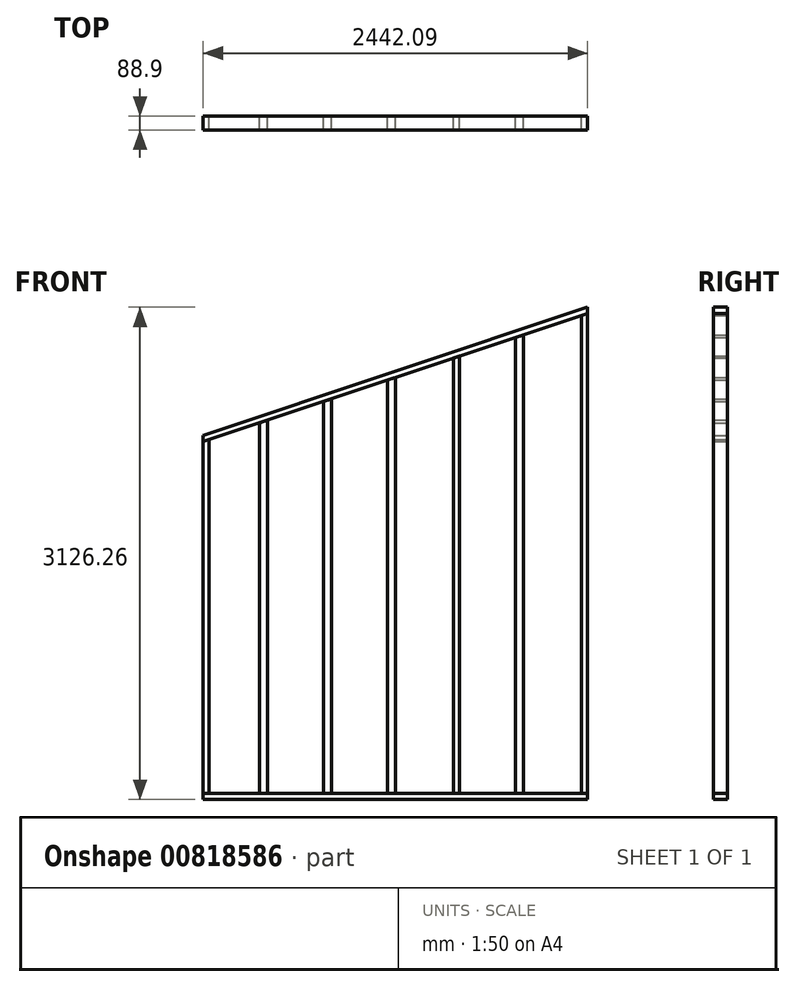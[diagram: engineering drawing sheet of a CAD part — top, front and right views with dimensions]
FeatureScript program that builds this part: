
annotation { "Feature Type Name" : "Feature", "Feature Type Description" : "" }
export const myFeature = defineFeature(function(context is Context, id is Id, definition is map)
    precondition{}
    {
        {
            var Q0;
            Q0=qCreatedBy(makeId("Front.planeOp"),FACE);
            var sketch = newSketch(context, id + "F0", { "sketchPlane" : qUnion([Q0])});
            skPoint(sketch, "E0", {"position": v(1489.55, 1139.12) * mm});
            skLineSegment(sketch, "E1", {"start": v(-952.54, 325.1) * mm, "end": v(1489.55, 1139.12) * mm});
            skLineSegment(sketch, "E2", {"start": v(1489.55, 1139.12) * mm, "end": v(1489.55, -1987.14) * mm});
            skLineSegment(sketch, "E3.0", {"start": v(-952.54, 284.93) * mm, "end": v(1489.55, 1098.96) * mm});
            skLineSegment(sketch, "E3.1", {"start": v(1451.45, 1086.26) * mm, "end": v(1451.45, -1949.04) * mm});
            skLineSegment(sketch, "E4.trimOffspring", {"start": v(1083.15, 963.5) * mm, "end": v(1083.15, -1949.04) * mm});
            skLineSegment(sketch, "E5.trimOffspring", {"start": v(1032.35, 946.56) * mm, "end": v(1032.35, -1949.04) * mm});
            skLineSegment(sketch, "E6.trimOffspring", {"start": v(676.75, 828.03) * mm, "end": v(676.75, -1949.04) * mm});
            skLineSegment(sketch, "E7.trimOffspring", {"start": v(219.55, 675.63) * mm, "end": v(219.55, -1949.04) * mm});
            skLineSegment(sketch, "E8.trimOffspring", {"start": v(270.35, 692.56) * mm, "end": v(270.35, -1949.04) * mm});
            skLineSegment(sketch, "E9.trimOffspring", {"start": v(-136.05, 557.1) * mm, "end": v(-136.05, -1949.04) * mm});
            skLineSegment(sketch, "E10.trimOffspring", {"start": v(-186.85, 540.16) * mm, "end": v(-186.85, -1949.04) * mm});
            skLineSegment(sketch, "E11.trimOffspring", {"start": v(-542.45, 421.63) * mm, "end": v(-542.45, -1949.04) * mm});
            skLineSegment(sketch, "E12.trimOffspring", {"start": v(-593.25, 404.7) * mm, "end": v(-593.25, -1949.04) * mm});
            skLineSegment(sketch, "E13.0", {"start": v(1489.55, -1949.04) * mm, "end": v(-952.54, -1949.04) * mm});
            skLineSegment(sketch, "E14.0", {"start": v(1489.55, -1987.14) * mm, "end": v(-952.54, -1987.14) * mm});
            skLineSegment(sketch, "E15.trimOffspring", {"start": v(-952.54, -1987.14) * mm, "end": v(-952.54, 325.1) * mm});
            skLineSegment(sketch, "E16.0", {"start": v(638.65, 815.33) * mm, "end": v(638.65, -1949.04) * mm});
            skLineSegment(sketch, "E17.0", {"start": v(-914.44, -1949.04) * mm, "end": v(-914.44, 297.63) * mm});
            skSolve(sketch);
        }
        {
            var Q0;
            {var subQ5=sQuery(id+"F0.wireOp",EDGE,"E3.1");Q0=makeQuery(id+"F0.imprint","IMPRINT",FACE,{"disambiguationData":[TD([[makeQuery(id+"F0.imprint","IMPRINT",EDGE,{"derivedFrom":subQ5}),1.0]])]});}
            var Q1;
            {var subQ3=sQuery(id+"F0.wireOp",EDGE,"E15.trimOffspring");Q1=makeQuery(id+"F0.imprint","IMPRINT",FACE,{"disambiguationData":[TD([[makeQuery(id+"F0.imprint","IMPRINT",EDGE,{"derivedFrom":subQ3}),1.0]])]});}
            var Q2;
            {var subQ0=sQuery(id+"F0.wireOp",EDGE,"E11.trimOffspring");Q2=makeQuery(id+"F0.imprint","IMPRINT",FACE,{"disambiguationData":[TD([[makeQuery(id+"F0.imprint","IMPRINT",EDGE,{"derivedFrom":subQ0}),-1.0]])]});}
            var Q3;
            {var subQ0=sQuery(id+"F0.wireOp",EDGE,"E9.trimOffspring");Q3=makeQuery(id+"F0.imprint","IMPRINT",FACE,{"disambiguationData":[TD([[makeQuery(id+"F0.imprint","IMPRINT",EDGE,{"derivedFrom":subQ0}),-1.0]])]});}
            var Q4;
            {var subQ0=sQuery(id+"F0.wireOp",EDGE,"E7.trimOffspring");Q4=makeQuery(id+"F0.imprint","IMPRINT",FACE,{"disambiguationData":[TD([[makeQuery(id+"F0.imprint","IMPRINT",EDGE,{"derivedFrom":subQ0}),1.0]])]});}
            var Q5;
            {var subQ0=sQuery(id+"F0.wireOp",EDGE,"E6.trimOffspring");Q5=makeQuery(id+"F0.imprint","IMPRINT",FACE,{"disambiguationData":[TD([[makeQuery(id+"F0.imprint","IMPRINT",EDGE,{"derivedFrom":subQ0}),-1.0]])]});}
            var Q6;
            {var subQ0=sQuery(id+"F0.wireOp",EDGE,"E4.trimOffspring");Q6=makeQuery(id+"F0.imprint","IMPRINT",FACE,{"disambiguationData":[TD([[makeQuery(id+"F0.imprint","IMPRINT",EDGE,{"derivedFrom":subQ0}),-1.0]])]});}
            var Q7;
            {var subQ3=sQuery(id+"F0.wireOp",EDGE,"E17.0");Q7=makeQuery(id+"F0.imprint","IMPRINT",FACE,{"disambiguationData":[TD([[makeQuery(id+"F0.imprint","IMPRINT",EDGE,{"derivedFrom":subQ3}),1.0]])]});}
            extrude(context, id + "F1", {"entities" : qUnion([Q0, Q1, Q2, Q3, Q4, Q5, Q6, Q7]), "depth" : 88.9 * mm, "offsetDistance" : 25.4 * mm});
        }
        {
            var Q0;
            {var subQ8=sQuery(id+"F0.wireOp",EDGE,"E1");Q0=makeQuery(id+"F0.imprint","IMPRINT",FACE,{"disambiguationData":[TD([[makeQuery(id+"F0.imprint","IMPRINT",EDGE,{"derivedFrom":subQ8}),-1.0]])]});}
            var Q1;
            {var subQ8=sQuery(id+"F0.wireOp",EDGE,"E14.0");Q1=makeQuery(id+"F0.imprint","IMPRINT",FACE,{"disambiguationData":[TD([[makeQuery(id+"F0.imprint","IMPRINT",EDGE,{"derivedFrom":subQ8}),-1.0]])]});}
            extrude(context, id + "F2", {"entities" : qUnion([Q0, Q1]), "depth" : 88.9 * mm, "offsetDistance" : 25.4 * mm});
        }
    });
